# Revit family: Haworth_ActiveComponents_RectangleScreenConvergent
name_source: partatom
category: Furniture Systems
revit_build: Autodesk Revit 2018 (Build: 20170223_1515(x64)
units: mm (PartAtom-declared; Revit-internal decimal feet)

## family parameters
Always vertical = Yes
Cut with Voids When Loaded = No
OmniClass Number = 23.40.70.14.64.21
OmniClass Title = Systems Furniture
Part Type = Normal
Room Calculation Point = No
Round Connector Dimension = Use Diameter
Shared = No
Work Plane-Based = No

## types (4) — shared parameters
Actual Height = 29.188 "
Angled Leg Offset = 3.25 "
Assembly Code = E2020200
Description = Haworth - Active Components - Rectangular Screen Convergent
Leg F/B Offset = 8.125 "
Manufacturer = Haworth
Max. Depth = 30 "
Max. Width = 72 "
Min. Depth = 24 "
Min. Width = 60 "
Model = WAYR
Radius = 3 "
Revision Number = 1
Screen Mounting Height = 28 "
Screen Offset = 5.938 "
Size = Verify Final Dim. w/ Haworth
Thickness = 1.188 "
Trim Finish = Haworth _ Paint _ Charcoal
URL = www.haworth.com
URL - Product = https://www.haworth.com
Warranty = https://www.haworth.com
With Leg = Yes

## per-type parameters (varying)
| type | Actual Depth | Actual Width | Depth | Overhang | Screen Width | Width |
| 30d 72w - 48 Center Screen | 30 " | 72 " | 30 " | 24 " | 48 " | 72 " |
| 30d 60w - 42 Center Screen | 30 " | 60 " | 30 " | 18 " | 42 " | 60 " |
| 24d 72w - 48 Center Screen | 24 " | 72 " | 24 " | 24 " | 48 " | 72 " |
| 24d 60w - 42 Center Screen | 24 " | 60 " | 24 " | 18 " | 42 " | 60 " |

## geometry (parser evidence)
native form markers: Sweep x16
no freeform markers — native parametric forms only
